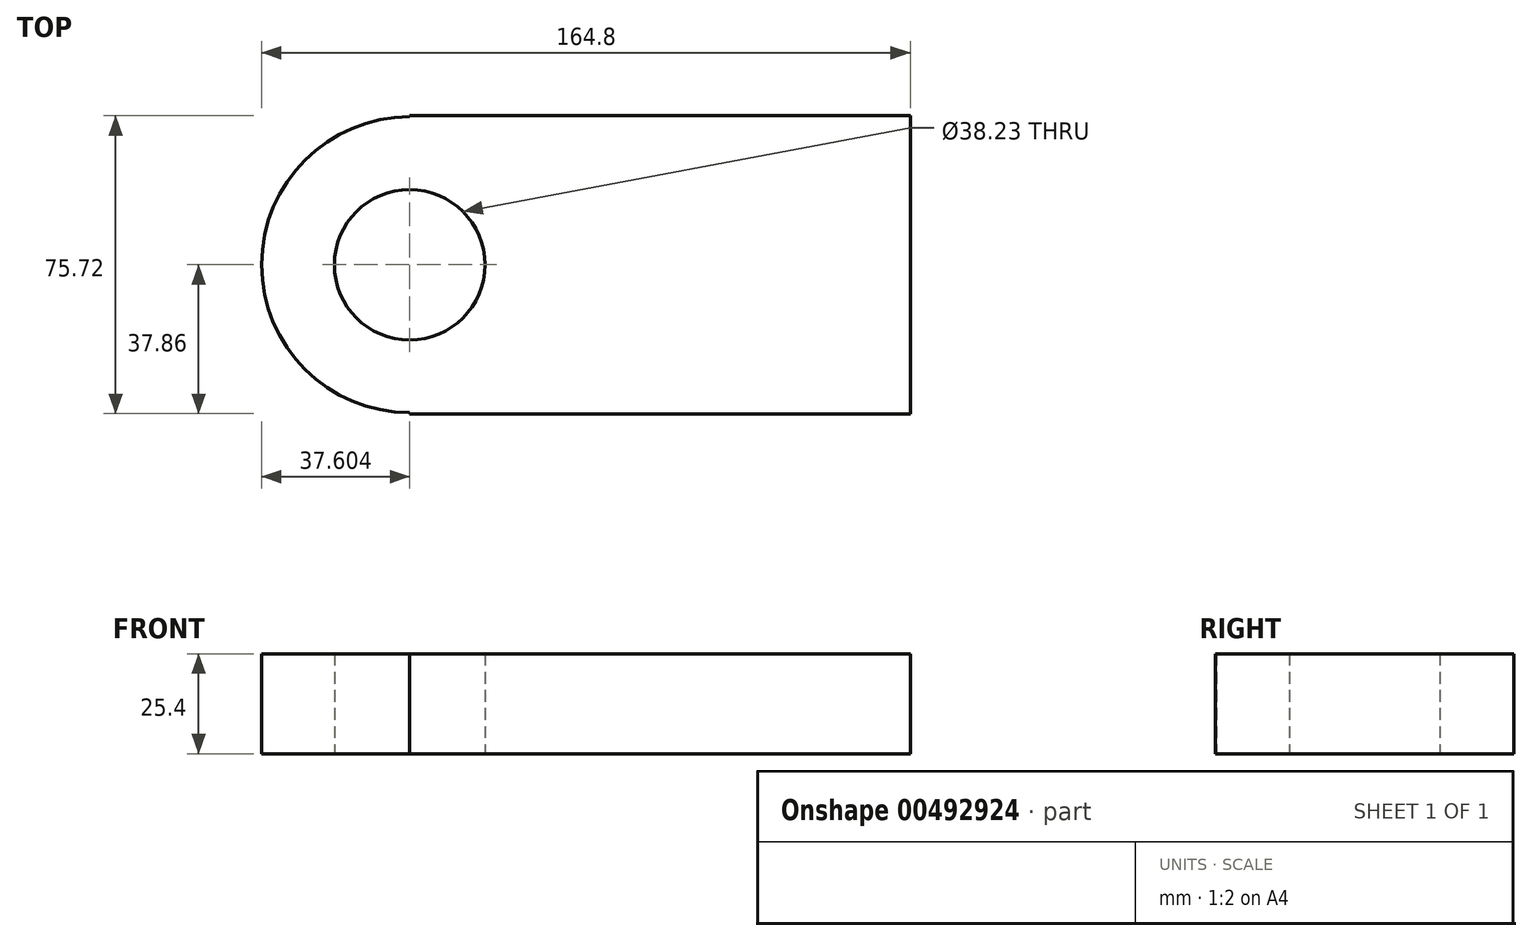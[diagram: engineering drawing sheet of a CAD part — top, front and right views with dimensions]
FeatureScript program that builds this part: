
annotation { "Feature Type Name" : "Feature", "Feature Type Description" : "" }
export const myFeature = defineFeature(function(context is Context, id is Id, definition is map)
    precondition{}
    {
        {
            var Q0;
            Q0=qCreatedBy(makeId("Top.planeOp"),FACE);
            var sketch = newSketch(context, id + "F0", { "sketchPlane" : qUnion([Q0])});
            skLineSegment(sketch, "E0.bottom", {"start": v(-63.6, -37.86) * mm, "end": v(63.6, -37.86) * mm});
            skLineSegment(sketch, "E0.top", {"start": v(-63.6, 37.86) * mm, "end": v(63.6, 37.86) * mm});
            skLineSegment(sketch, "E0.left", {"start": v(-63.6, -37.86) * mm, "end": v(-63.6, 37.86) * mm});
            skLineSegment(sketch, "E0.right", {"start": v(63.6, -37.86) * mm, "end": v(63.6, 37.86) * mm});
            skPoint(sketch, "E0.middle", {"position": v(0, 0) * mm});
            skCircle(sketch, "E1", {"center": v(-63.6, 0) * mm, "radius": 37.6 * mm});
            skCircle(sketch, "E2", {"center": v(-63.6, 0) * mm, "radius": 19.11 * mm});
            skSolve(sketch);
        }
        {
            var Q0;
            Q0 = qSketchRegion(id + "F0", true);
            extrude(context, id + "F1", {"entities" : qUnion([Q0]), "depth" : 25.4 * mm});
        }
    });
